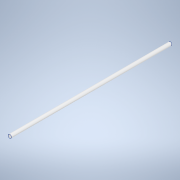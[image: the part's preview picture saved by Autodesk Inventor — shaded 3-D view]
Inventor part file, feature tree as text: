
AUTODESK INVENTOR PART (.ipt)
format: ipt  version: 2020.3 (Build 243373000, 373)  size: 91,136 bytes
history: native  units: mm
features: extrude x1, sketch x1
ambient origin geometry x8: Origin, YZ Plane, XZ Plane, XY Plane, X Axis, Y Axis, Z Axis, Center Point
bodies: Solid1 (feature_tree)
feature tree (2):
  extrude  "Extrusion1"  Depth=300.0mm TaperAngle=0.0deg
  sketch  "Sketch1"  dims[d0=6.5mm d1=300.0mm d2=0.0mm]
